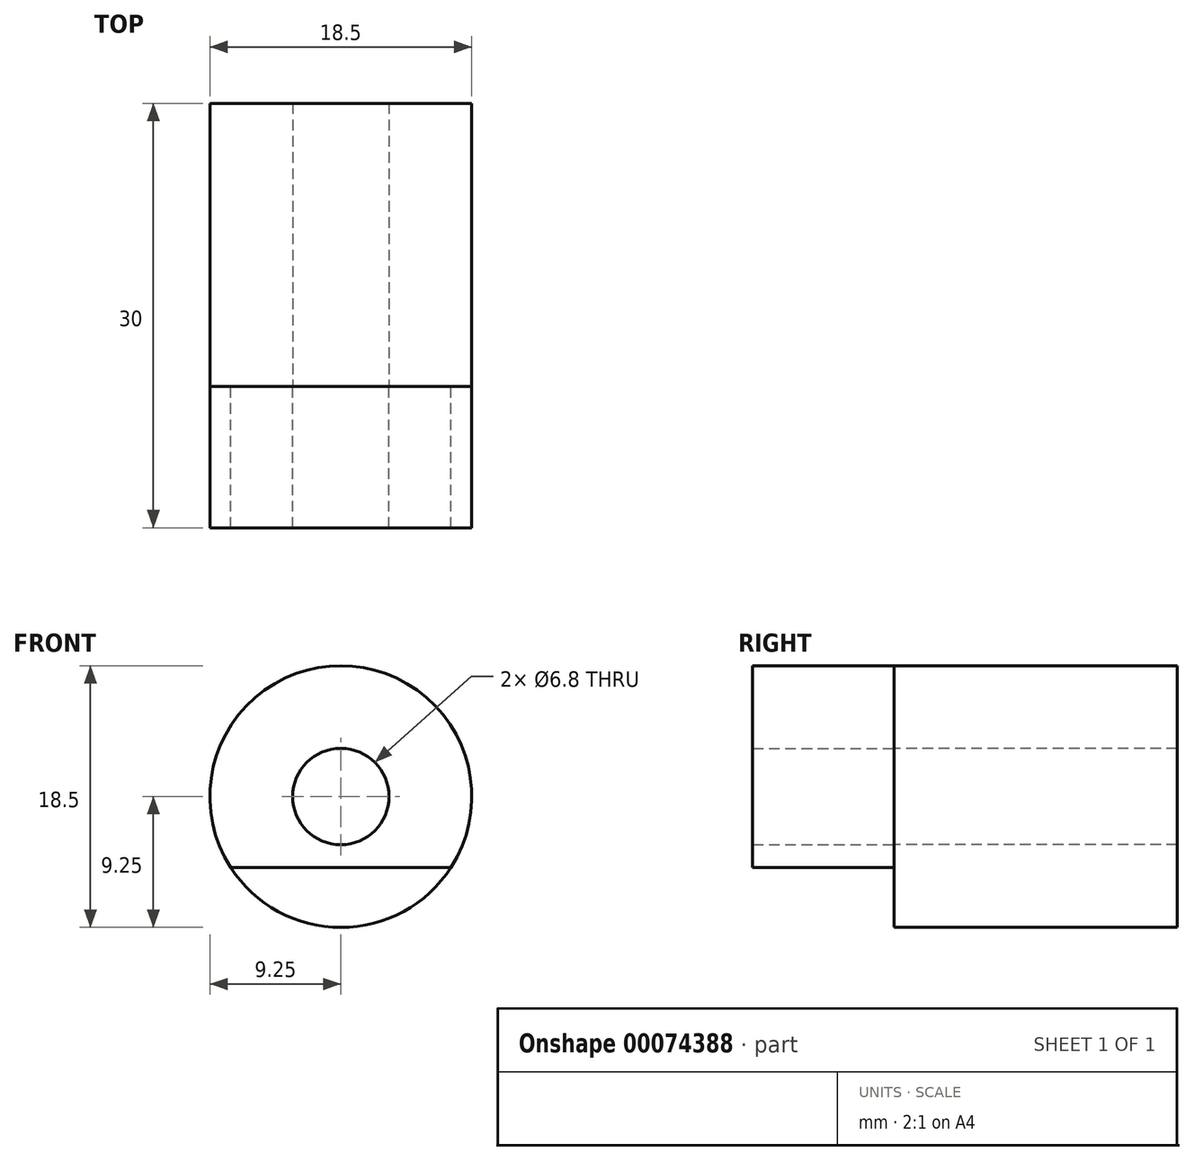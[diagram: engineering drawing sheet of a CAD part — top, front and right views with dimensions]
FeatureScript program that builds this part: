
annotation { "Feature Type Name" : "Feature", "Feature Type Description" : "" }
export const myFeature = defineFeature(function(context is Context, id is Id, definition is map)
    precondition{}
    {
        {
            var Q0;
            Q0=qCreatedBy(makeId("Front.planeOp"),FACE);
            var sketch = newSketch(context, id + "F0", { "sketchPlane" : qUnion([Q0])});
            skCircle(sketch, "E0", {"center": v(0, 0) * mm, "radius": 9.25 * mm});
            skCircle(sketch, "E1", {"center": v(0, 0) * mm, "radius": 3.4 * mm});
            skLineSegment(sketch, "E2", {"start": v(-7.78, -5) * mm, "end": v(7.78, -5) * mm});
            skSolve(sketch);
        }
        {
            var Q0;
            Q0=makeQuery(id+"F0.imprint","IMPRINT",FACE,{"disambiguationData":[TD([[makeQuery(id+"F0.imprint","IMPRINT",EDGE,{"derivedFrom":sQuery(id+"F0.wireOp",EDGE,"E1")}),-1.0]])]});
            var Q1;
            {var subQ0=sQuery(id+"F0.wireOp",EDGE,"E2");Q1=makeQuery(id+"F0.imprint","IMPRINT",FACE,{"disambiguationData":[TD([[makeQuery(id+"F0.imprint","IMPRINT",EDGE,{"derivedFrom":subQ0}),-1.0]])]});}
            extrude(context, id + "F1", {"entities" : qUnion([Q0, Q1]), "oppositeDirection" : true, "depth" : 20 * mm});
        }
        {
            var Q0;
            Q0=makeQuery(id+"F0.imprint","IMPRINT",FACE,{"disambiguationData":[TD([[makeQuery(id+"F0.imprint","IMPRINT",EDGE,{"derivedFrom":sQuery(id+"F0.wireOp",EDGE,"E1")}),-1.0]])]});
            extrude(context, id + "F2", {"entities" : qUnion([Q0]), "depth" : 10 * mm});
        }
    });
